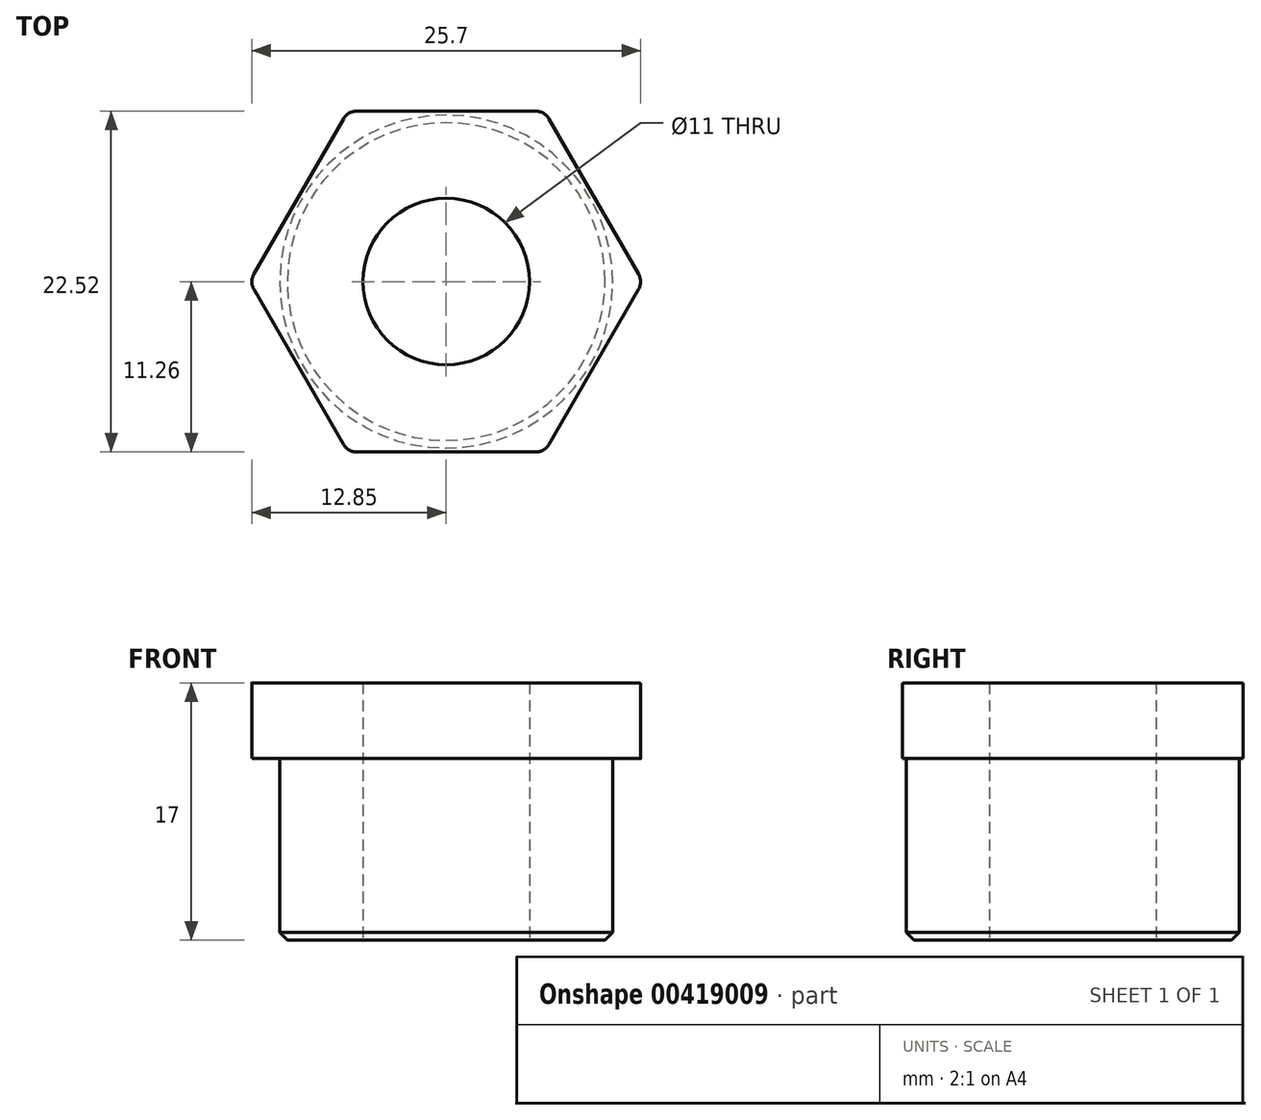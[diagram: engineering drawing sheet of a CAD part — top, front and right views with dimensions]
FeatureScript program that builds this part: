
annotation { "Feature Type Name" : "Feature", "Feature Type Description" : "" }
export const myFeature = defineFeature(function(context is Context, id is Id, definition is map)
    precondition{}
    {
        {
            var Q0;
            Q0=qCreatedBy(makeId("Top.planeOp"),FACE);
            var sketch = newSketch(context, id + "F0", { "sketchPlane" : qUnion([Q0])});
            skCircle(sketch, "E0.cCircle", {"center": v(0, 0) * mm, "radius": 11.26 * mm, "construction": true});
            skLineSegment(sketch, "E0.0", {"start": v(-6.5, 11.26) * mm, "end": v(6.5, 11.26) * mm});
            skLineSegment(sketch, "E0.1", {"start": v(6.5, 11.26) * mm, "end": v(13, 0) * mm});
            skLineSegment(sketch, "E0.2", {"start": v(13, 0) * mm, "end": v(6.5, -11.26) * mm});
            skLineSegment(sketch, "E0.3", {"start": v(6.5, -11.26) * mm, "end": v(-6.5, -11.26) * mm});
            skLineSegment(sketch, "E0.4", {"start": v(-6.5, -11.26) * mm, "end": v(-13, 0) * mm});
            skLineSegment(sketch, "E0.5", {"start": v(-13, 0) * mm, "end": v(-6.5, 11.26) * mm});
            skPoint(sketch, "E0.0.midPoint", {"position": v(0, 11.26) * mm});
            skSolve(sketch);
        }
        {
            var Q0;
            Q0 = qSketchRegion(id + "F0", true);
            extrude(context, id + "F1", {"entities" : qUnion([Q0]), "oppositeDirection" : true, "depth" : 5 * mm});
        }
        {
            var Q0;
            Q0=makeQuery(id+"F1.opExtrude","SWEPT_EDGE",EDGE,{"disambiguationData":[OSD([sQuery(id+"F0.wireOp",EDGE,"E0.2"),sQuery(id+"F0.wireOp",EDGE,"E0.3")])]});
            var Q1;
            Q1=makeQuery(id+"F1.opExtrude","SWEPT_EDGE",EDGE,{"disambiguationData":[OSD([sQuery(id+"F0.wireOp",EDGE,"E0.3"),sQuery(id+"F0.wireOp",EDGE,"E0.4")])]});
            var Q2;
            Q2=makeQuery(id+"F1.opExtrude","SWEPT_EDGE",EDGE,{"disambiguationData":[OSD([sQuery(id+"F0.wireOp",EDGE,"E0.4"),sQuery(id+"F0.wireOp",EDGE,"E0.5")])]});
            var Q3;
            Q3=makeQuery(id+"F1.opExtrude","SWEPT_EDGE",EDGE,{"disambiguationData":[OSD([sQuery(id+"F0.wireOp",EDGE,"E0.1"),sQuery(id+"F0.wireOp",EDGE,"E0.2")])]});
            var Q4;
            Q4=makeQuery(id+"F1.opExtrude","SWEPT_EDGE",EDGE,{"disambiguationData":[OSD([sQuery(id+"F0.wireOp",EDGE,"E0.0"),sQuery(id+"F0.wireOp",EDGE,"E0.1")])]});
            var Q5;
            Q5=makeQuery(id+"F1.opExtrude","SWEPT_EDGE",EDGE,{"disambiguationData":[OSD([sQuery(id+"F0.wireOp",EDGE,"E0.0"),sQuery(id+"F0.wireOp",EDGE,"E0.5")])]});
            fillet(context, id + "F2", {"entities" : qUnion([Q0, Q1, Q2, Q3, Q4, Q5]), "radius" : 1 * mm, "tangentPropagation" : true, "allowEdgeOverflow" : false});
        }
        {
            var Q0;
            Q0=makeQuery(id+"F1.opExtrude","CAP_FACE",FACE,{"disambiguationData":[OSD([sQuery(id+"F0.wireOp",EDGE,"E0.0"),sQuery(id+"F0.wireOp",EDGE,"E0.1"),sQuery(id+"F0.wireOp",EDGE,"E0.2"),sQuery(id+"F0.wireOp",EDGE,"E0.3"),sQuery(id+"F0.wireOp",EDGE,"E0.4"),sQuery(id+"F0.wireOp",EDGE,"E0.5")])],"isStart":false});
            cPlane(context, id + "F3", {"entities" : qUnion([Q0]), "cplaneType" : CPlaneType.OFFSET, "offset" : 0 * mm, "width" : 150 * mm, "height" : 150 * mm});
        }
        {
            var Q0;
            Q0=qCreatedBy(id+"F3.planeOp",FACE);
            var sketch = newSketch(context, id + "F4", { "sketchPlane" : qUnion([Q0])});
            skCircle(sketch, "E1", {"center": v(0, 0) * mm, "radius": 11 * mm});
            skSolve(sketch);
        }
        {
            var Q0;
            Q0=makeQuery(id+"F4.imprint","IMPRINT",FACE,{"disambiguationData":[TD([[makeQuery(id+"F4.imprint","IMPRINT",EDGE,{"derivedFrom":sQuery(id+"F4.wireOp",EDGE,"E1")}),1.0]])]});
            extrude(context, id + "F5", {"entities" : qUnion([Q0]), "operationType" : NewBodyOperationType.ADD, "depth" : 12 * mm});
        }
        {
            var Q0;
            Q0=makeQuery(id+"F5.opExtrude","CAP_EDGE",EDGE,{"disambiguationData":[OSD([sQuery(id+"F4.wireOp",EDGE,"E1")])],"isStart":false});
            chamfer(context, id + "F6", {"entities" : qUnion([Q0]), "width" : 0.5 * mm, "tangentPropagation" : true});
        }
        {
            var Q0;
            Q0=makeQuery(id+"F5.opExtrude","CAP_FACE",FACE,{"disambiguationData":[OSD([sQuery(id+"F4.wireOp",EDGE,"E1")])],"isStart":false});
            var sketch = newSketch(context, id + "F7", { "sketchPlane" : qUnion([Q0])});
            skCircle(sketch, "E2", {"center": v(0, 0) * mm, "radius": 5.5 * mm});
            skSolve(sketch);
        }
        {
            var Q0;
            Q0=makeQuery(id+"F7.imprint","IMPRINT",FACE,{"disambiguationData":[TD([[makeQuery(id+"F7.imprint","IMPRINT",EDGE,{"derivedFrom":sQuery(id+"F7.wireOp",EDGE,"E2")}),1.0]])]});
            extrude(context, id + "F8", {"entities" : qUnion([Q0]), "operationType" : NewBodyOperationType.REMOVE, "endBound" : BoundingType.THROUGH_ALL, "oppositeDirection" : true, "depth" : 25 * mm});
        }
    });
